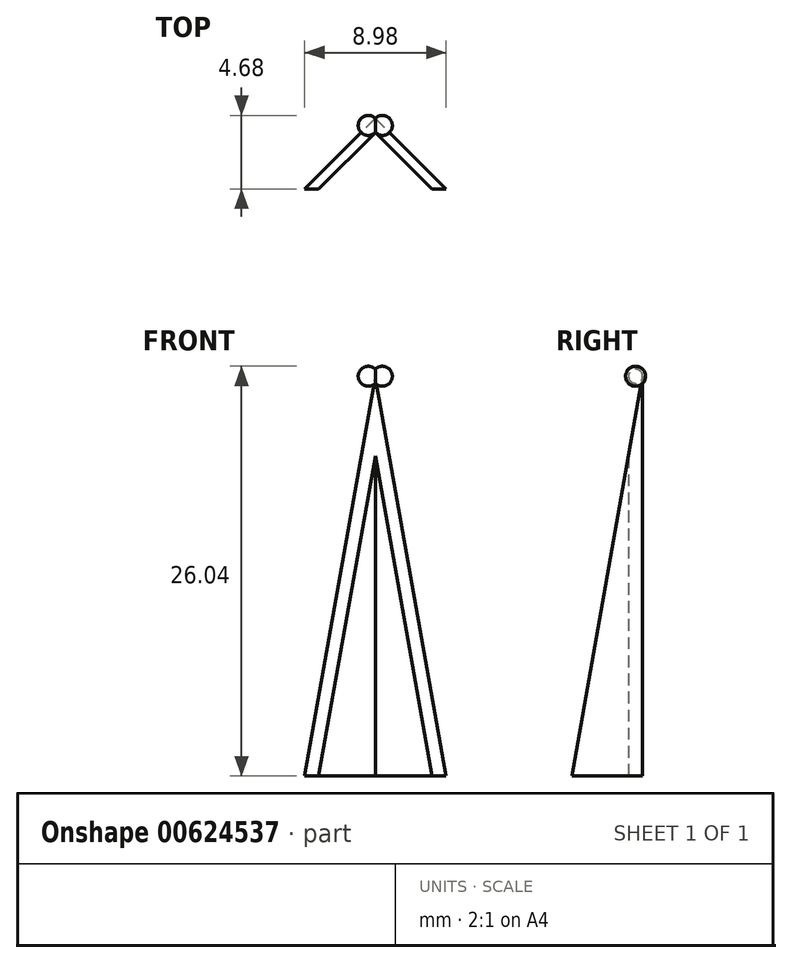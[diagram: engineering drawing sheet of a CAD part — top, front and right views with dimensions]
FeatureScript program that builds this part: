
annotation { "Feature Type Name" : "Feature", "Feature Type Description" : "" }
export const myFeature = defineFeature(function(context is Context, id is Id, definition is map)
    precondition{}
    {
        {
            var Q0;
            Q0=qCreatedBy(makeId("Top.planeOp"),FACE);
            var sketch = newSketch(context, id + "F0", { "sketchPlane" : qUnion([Q0])});
            skLineSegment(sketch, "E0.bottom", {"start": v(0, 4.5) * mm, "end": v(-4.5, 0) * mm});
            skLineSegment(sketch, "E0.top", {"start": v(4.5, 0) * mm, "end": v(0, -4.5) * mm});
            skLineSegment(sketch, "E0.left", {"start": v(0, 4.5) * mm, "end": v(4.5, 0) * mm});
            skLineSegment(sketch, "E0.right", {"start": v(-4.5, 0) * mm, "end": v(0, -4.5) * mm});
            skPoint(sketch, "E0.middle", {"position": v(0, 0) * mm});
            skSolve(sketch);
        }
        {
            var Q0;
            Q0=qCreatedBy(makeId("Top.planeOp"),FACE);
            var sketch = newSketch(context, id + "F1", { "sketchPlane" : qUnion([Q0])});
            skLineSegment(sketch, "E1.0", {"start": v(0, 3.6) * mm, "end": v(-3.6, 0) * mm});
            skLineSegment(sketch, "E1.1", {"start": v(0, 3.6) * mm, "end": v(3.6, 0) * mm});
            skLineSegment(sketch, "E1.2", {"start": v(3.6, 0) * mm, "end": v(0, -3.6) * mm});
            skLineSegment(sketch, "E1.3", {"start": v(-3.6, 0) * mm, "end": v(0, -3.6) * mm});
            skSolve(sketch);
        }
        {
            var Q0;
            Q0=qCreatedBy(makeId("Top.planeOp"),FACE);
            var sketch = newSketch(context, id + "F2", { "sketchPlane" : qUnion([Q0])});
            skLineSegment(sketch, "E2.bottom", {"start": v(-4.49, 0) * mm, "end": v(4.49, 0) * mm});
            skLineSegment(sketch, "E2.top", {"start": v(-4.49, 8.98) * mm, "end": v(4.49, 8.98) * mm});
            skLineSegment(sketch, "E2.left", {"start": v(-4.49, 0) * mm, "end": v(-4.49, 8.98) * mm});
            skLineSegment(sketch, "E2.right", {"start": v(4.49, 0) * mm, "end": v(4.49, 8.98) * mm});
            skPoint(sketch, "E2.middle", {"position": v(0, 4.5) * mm});
            skSolve(sketch);
        }
        {
            var Q0;
            Q0 = qSketchRegion(id + "F0", true);
            extrude(context, id + "F3", {"entities" : qUnion([Q0]), "depth" : 25.4 * mm, "offsetDistance" : 25.4 * mm});
        }
        {
            var Q0;
            Q0 = qSketchRegion(id + "F1", true);
            extrude(context, id + "F4", {"entities" : qUnion([Q0]), "operationType" : NewBodyOperationType.REMOVE, "depth" : 25.4 * mm, "offsetDistance" : 25.4 * mm});
        }
        {
            var Q0;
            Q0 = qSketchRegion(id + "F2", true);
            extrude(context, id + "F5", {"entities" : qUnion([Q0]), "operationType" : NewBodyOperationType.INTERSECT, "depth" : 25.4 * mm, "offsetDistance" : 25.4 * mm});
        }
        {
            var Q0;
            Q0=qCreatedBy(makeId("Right.planeOp"),FACE);
            var sketch = newSketch(context, id + "F6", { "sketchPlane" : qUnion([Q0])});
            skLineSegment(sketch, "E3", {"start": v(0, 0) * mm, "end": v(4.5, 25.4) * mm});
            skLineSegment(sketch, "E4", {"start": v(4.5, 25.4) * mm, "end": v(4.5, 0) * mm});
            skLineSegment(sketch, "E5", {"start": v(4.5, 0) * mm, "end": v(0, 0) * mm});
            skSolve(sketch);
        }
        {
            var Q0;
            Q0 = qSketchRegion(id + "F6", true);
            extrude(context, id + "F7", {"entities" : qUnion([Q0]), "operationType" : NewBodyOperationType.INTERSECT, "depth" : 6.35 * mm, "offsetDistance" : 25.4 * mm, "hasSecondDirection" : true, "secondDirectionOppositeDirection" : true, "secondDirectionDepth" : 6.35 * mm});
        }
        {
            var Q0;
            Q0=qCreatedBy(makeId("Right.planeOp"),FACE);
            var sketch = newSketch(context, id + "F8", { "sketchPlane" : qUnion([Q0])});
            skArc(sketch, "E6", {"start": v(4.5, 25.4) * mm, "mid": v(2.93, 24.09) * mm, "end": v(3.95, 22.32) * mm});
            skArc(sketch, "E7", {"start": v(3.95, 22.32) * mm, "mid": v(6.05, 23.54) * mm, "end": v(4.5, 25.4) * mm});
            skSolve(sketch);
        }
        {
            var Q0;
            Q0=qCreatedBy(makeId("Right.planeOp"),FACE);
            var sketch = newSketch(context, id + "F9", { "sketchPlane" : qUnion([Q0])});
            skLineSegment(sketch, "E8.bottom", {"start": v(4.5, 25.4) * mm, "end": v(1.63, 25.4) * mm});
            skLineSegment(sketch, "E8.top", {"start": v(4.5, 22.23) * mm, "end": v(1.63, 22.23) * mm});
            skLineSegment(sketch, "E8.left", {"start": v(4.5, 25.4) * mm, "end": v(4.5, 22.23) * mm});
            skLineSegment(sketch, "E8.right", {"start": v(1.63, 25.4) * mm, "end": v(1.63, 22.23) * mm});
            skSolve(sketch);
        }
        {
            var Q0;
            Q0=qCreatedBy(makeId("Top.planeOp"),FACE);
            cPlane(context, id + "F10", {"entities" : qUnion([Q0]), "cplaneType" : CPlaneType.OFFSET, "offset" : 25.4 * mm, "width" : 152.4 * mm, "height" : 152.4 * mm});
        }
        {
            var Q0;
            Q0=qCreatedBy(id+"F10.planeOp",FACE);
            var sketch = newSketch(context, id + "F11", { "sketchPlane" : qUnion([Q0])});
            skCircle(sketch, "E9", {"center": v(-0.45, 4.04) * mm, "radius": 0.64 * mm});
            skSolve(sketch);
        }
        {
            var Q0;
            Q0=qCreatedBy(id+"F10.planeOp",FACE);
            var sketch = newSketch(context, id + "F12", { "sketchPlane" : qUnion([Q0])});
            skCircle(sketch, "E10", {"center": v(0.45, 4.04) * mm, "radius": 0.64 * mm});
            skSolve(sketch);
        }
        {
            var Q0;
            Q0=qCreatedBy(id+"F10.planeOp",FACE);
            var sketch = newSketch(context, id + "F13", { "sketchPlane" : qUnion([Q0])});
            skLineSegment(sketch, "E11", {"start": v(-1.93, 4.04) * mm, "end": v(1.78, 4.04) * mm});
            skSolve(sketch);
        }
        {
            var Q0;
            Q0=qCreatedBy(id+"F10.planeOp",FACE);
            var sketch = newSketch(context, id + "F14", { "sketchPlane" : qUnion([Q0])});
            skArc(sketch, "E12", {"start": v(-1.08, 4.04) * mm, "mid": v(-0.45, 3.4) * mm, "end": v(0.19, 4.04) * mm});
            skLineSegment(sketch, "E13", {"start": v(-1.08, 4.04) * mm, "end": v(0.19, 4.04) * mm});
            skSolve(sketch);
        }
        {
            var Q0;
            Q0=qCreatedBy(id+"F10.planeOp",FACE);
            var sketch = newSketch(context, id + "F15", { "sketchPlane" : qUnion([Q0])});
            skArc(sketch, "E14", {"start": v(-0.19, 4.04) * mm, "mid": v(0.45, 3.4) * mm, "end": v(1.08, 4.04) * mm});
            skLineSegment(sketch, "E15", {"start": v(-0.19, 4.04) * mm, "end": v(1.08, 4.04) * mm});
            skSolve(sketch);
        }
        {
            var Q0;
            Q0=makeQuery(id+"F14.imprint","IMPRINT",FACE,{"disambiguationData":[TD([[makeQuery(id+"F14.imprint","IMPRINT",EDGE,{"derivedFrom":sQuery(id+"F14.wireOp",EDGE,"E12")}),1.0]])]});
            var Q1;
            Q1=sQuery(id+"F13.wireOp",EDGE,"E11");
            revolve(context, id + "F16", {"operationType" : NewBodyOperationType.ADD, "entities" : qUnion([Q0]), "axis" : qUnion([Q1]), "revolveType" : RevolveType.FULL});
        }
        {
            var Q0;
            Q0=makeQuery(id+"F15.imprint","IMPRINT",FACE,{"disambiguationData":[TD([[makeQuery(id+"F15.imprint","IMPRINT",EDGE,{"derivedFrom":sQuery(id+"F15.wireOp",EDGE,"E14")}),1.0]])]});
            var Q1;
            Q1=sQuery(id+"F15.wireOp",EDGE,"E15");
            revolve(context, id + "F17", {"operationType" : NewBodyOperationType.ADD, "entities" : qUnion([Q0]), "axis" : qUnion([Q1]), "revolveType" : RevolveType.FULL});
        }
    });
